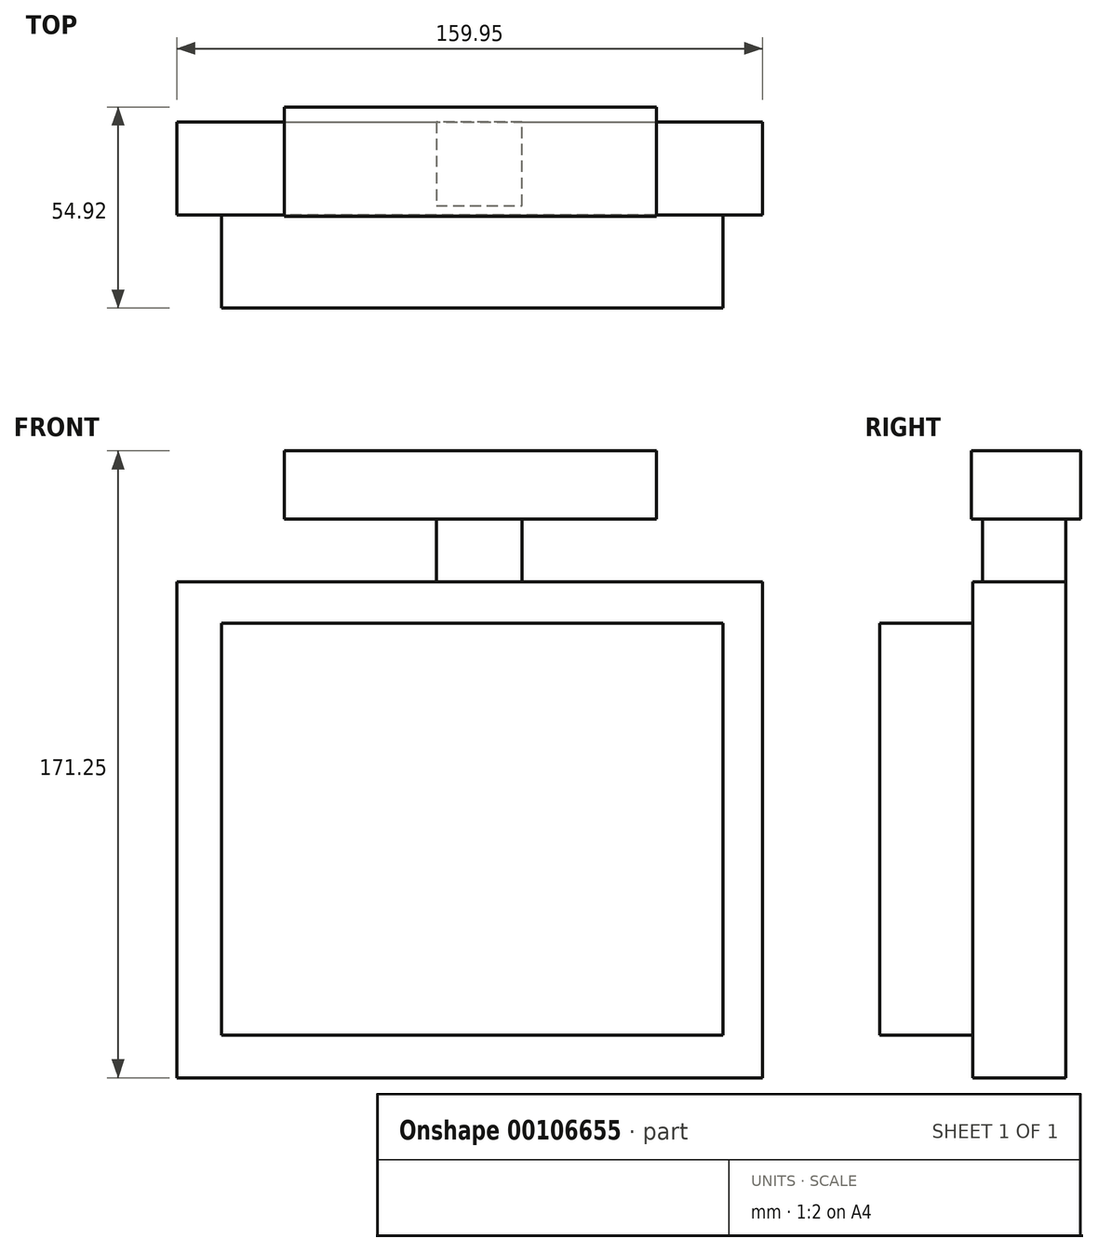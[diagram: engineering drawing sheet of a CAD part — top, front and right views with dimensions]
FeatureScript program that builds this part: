
annotation { "Feature Type Name" : "Feature", "Feature Type Description" : "" }
export const myFeature = defineFeature(function(context is Context, id is Id, definition is map)
    precondition{}
    {
        {
            var Q0;
            Q0=qCreatedBy(makeId("Front.planeOp"),FACE);
            var sketch = newSketch(context, id + "F0", { "sketchPlane" : qUnion([Q0])});
            skLineSegment(sketch, "E0.bottom", {"start": v(-80.24, 79.26) * mm, "end": v(79.71, 79.26) * mm});
            skLineSegment(sketch, "E0.top", {"start": v(-80.24, -56.2) * mm, "end": v(79.71, -56.2) * mm});
            skLineSegment(sketch, "E0.left", {"start": v(-80.24, 79.26) * mm, "end": v(-80.24, -56.2) * mm});
            skLineSegment(sketch, "E0.right", {"start": v(79.71, 79.26) * mm, "end": v(79.71, -56.2) * mm});
            skSolve(sketch);
        }
        {
            var Q0;
            Q0 = qSketchRegion(id + "F0", true);
            extrude(context, id + "F1", {"entities" : qUnion([Q0]), "depth" : 25.4 * mm});
        }
        {
            var Q0;
            Q0=qCreatedBy(makeId("Top.planeOp"),FACE);
            var sketch = newSketch(context, id + "F2", { "sketchPlane" : qUnion([Q0])});
            skLineSegment(sketch, "E1.bottom", {"start": v(-9.35, -22.79) * mm, "end": v(14.05, -22.79) * mm});
            skLineSegment(sketch, "E1.top", {"start": v(-9.35, 0) * mm, "end": v(14.05, 0) * mm});
            skLineSegment(sketch, "E1.left", {"start": v(-9.35, -22.79) * mm, "end": v(-9.35, 0) * mm});
            skLineSegment(sketch, "E1.right", {"start": v(14.05, -22.79) * mm, "end": v(14.05, 0) * mm});
            skSolve(sketch);
        }
        {
            var Q0;
            Q0 = qSketchRegion(id + "F2", true);
            extrude(context, id + "F3", {"entities" : qUnion([Q0]), "operationType" : NewBodyOperationType.ADD, "depth" : 101.6 * mm});
        }
        {
            var Q0;
            Q0=qCreatedBy(makeId("Right.planeOp"),FACE);
            var sketch = newSketch(context, id + "F4", { "sketchPlane" : qUnion([Q0])});
            skLineSegment(sketch, "E2.bottom", {"start": v(-25.8, 96.42) * mm, "end": v(4.12, 96.42) * mm});
            skLineSegment(sketch, "E2.top", {"start": v(-25.8, 115.05) * mm, "end": v(4.12, 115.05) * mm});
            skLineSegment(sketch, "E2.left", {"start": v(-25.8, 96.42) * mm, "end": v(-25.8, 115.05) * mm});
            skLineSegment(sketch, "E2.right", {"start": v(4.12, 96.42) * mm, "end": v(4.12, 115.05) * mm});
            skSolve(sketch);
        }
        {
            var Q0;
            Q0 = qSketchRegion(id + "F4", true);
            extrude(context, id + "F5", {"entities" : qUnion([Q0]), "operationType" : NewBodyOperationType.ADD, "depth" : 50.8 * mm});
        }
        {
            var Q0;
            Q0=qCreatedBy(makeId("Front.planeOp"),FACE);
            var sketch = newSketch(context, id + "F6", { "sketchPlane" : qUnion([Q0])});
            skLineSegment(sketch, "E3.bottom", {"start": v(-67.93, -44.58) * mm, "end": v(68.87, -44.58) * mm});
            skLineSegment(sketch, "E3.top", {"start": v(-67.93, 68) * mm, "end": v(68.87, 68) * mm});
            skLineSegment(sketch, "E3.left", {"start": v(-67.93, -44.58) * mm, "end": v(-67.93, 68) * mm});
            skLineSegment(sketch, "E3.right", {"start": v(68.87, -44.58) * mm, "end": v(68.87, 68) * mm});
            skSolve(sketch);
        }
        {
            var Q0;
            Q0 = qSketchRegion(id + "F6", true);
            extrude(context, id + "F7", {"entities" : qUnion([Q0]), "operationType" : NewBodyOperationType.ADD, "depth" : 50.8 * mm});
        }
        {
            var Q0;
            Q0=makeQuery(id+"F5.opExtrude","CAP_FACE",FACE,{"disambiguationData":[OSD([sQuery(id+"F4.wireOp",EDGE,"E2.bottom"),sQuery(id+"F4.wireOp",EDGE,"E2.top"),sQuery(id+"F4.wireOp",EDGE,"E2.left"),sQuery(id+"F4.wireOp",EDGE,"E2.right")])],"isStart":true});
            var sketch = newSketch(context, id + "F8", { "sketchPlane" : qUnion([Q0])});
            skLineSegment(sketch, "E4.bottom", {"start": v(25.8, 96.42) * mm, "end": v(-4.12, 96.42) * mm});
            skLineSegment(sketch, "E4.top", {"start": v(25.8, 115.05) * mm, "end": v(-4.12, 115.05) * mm});
            skLineSegment(sketch, "E4.left", {"start": v(25.8, 96.42) * mm, "end": v(25.8, 115.05) * mm});
            skLineSegment(sketch, "E4.right", {"start": v(-4.12, 96.42) * mm, "end": v(-4.12, 115.05) * mm});
            skSolve(sketch);
        }
        {
            var Q0;
            Q0 = qSketchRegion(id + "F8", true);
            extrude(context, id + "F9", {"entities" : qUnion([Q0]), "operationType" : NewBodyOperationType.ADD, "depth" : 50.8 * mm});
        }
    });
